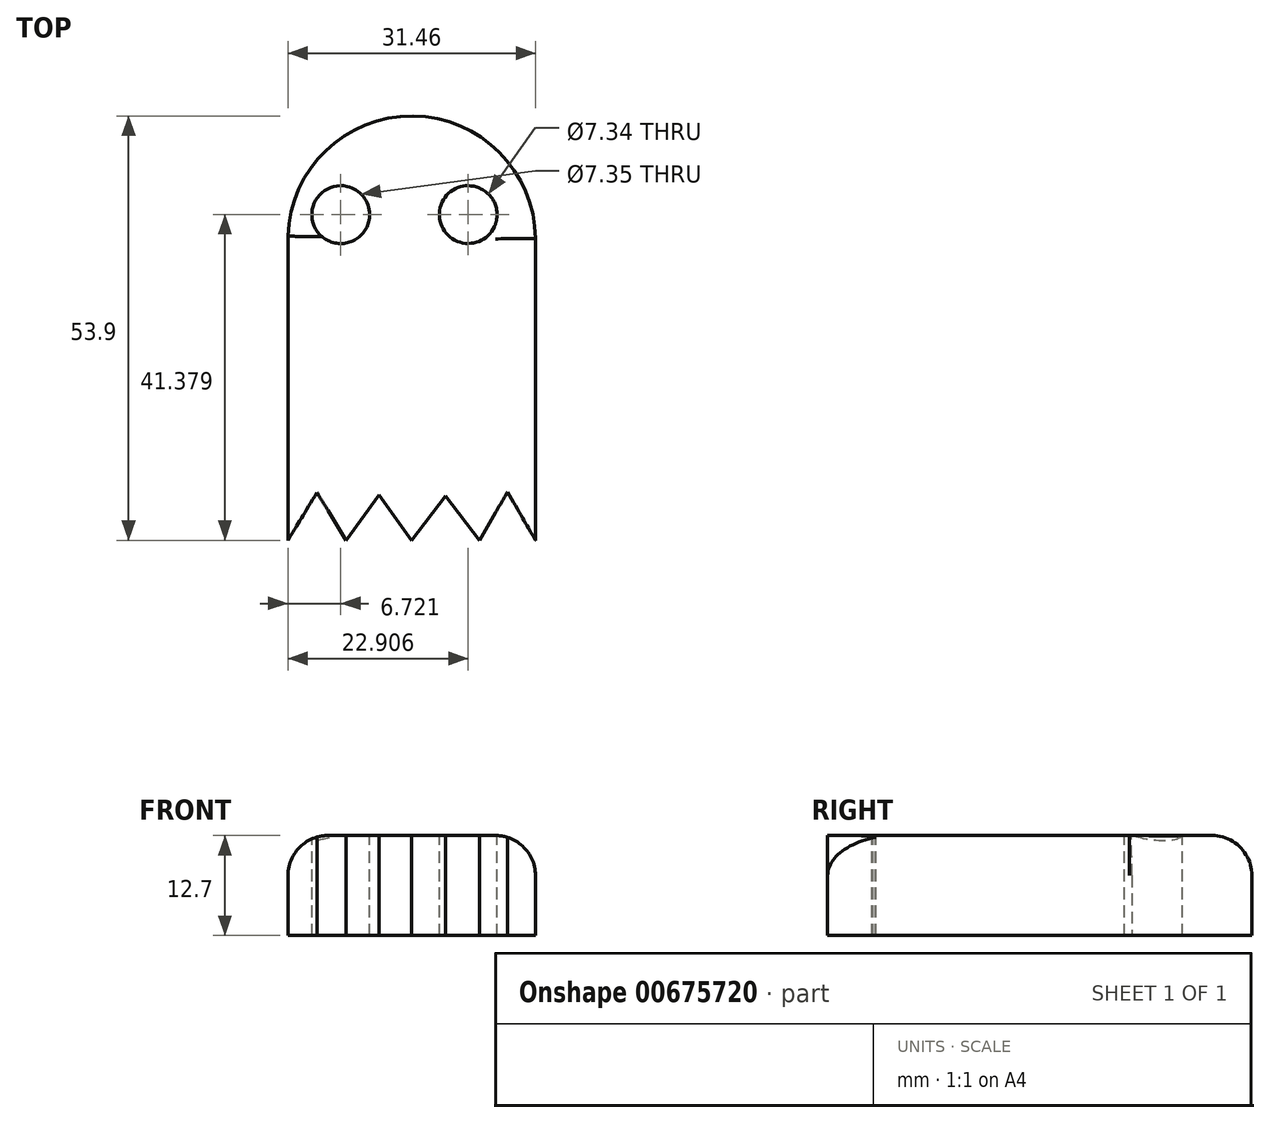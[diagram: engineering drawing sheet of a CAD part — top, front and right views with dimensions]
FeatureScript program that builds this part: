
annotation { "Feature Type Name" : "Feature", "Feature Type Description" : "" }
export const myFeature = defineFeature(function(context is Context, id is Id, definition is map)
    precondition{}
    {
        {
            var Q0;
            Q0=qCreatedBy(makeId("Top.planeOp"),FACE);
            var sketch = newSketch(context, id + "F0", { "sketchPlane" : qUnion([Q0])});
            skArc(sketch, "E0", {"start": v(-32.52, 38.33) * mm, "mid": v(-48.1, 53.9) * mm, "end": v(-63.98, 38.63) * mm});
            skLineSegment(sketch, "E1", {"start": v(-63.98, 38.63) * mm, "end": v(-63.98, 0) * mm});
            skLineSegment(sketch, "E2", {"start": v(-63.98, 0) * mm, "end": v(-32.52, 0) * mm});
            skLineSegment(sketch, "E3", {"start": v(-32.52, 0) * mm, "end": v(-32.52, 38.33) * mm});
            skSolve(sketch);
        }
        {
            var Q0;
            Q0=makeQuery(id+"F0.imprint","IMPRINT",FACE,{"disambiguationData":[TD([[makeQuery(id+"F0.imprint","IMPRINT",EDGE,{"derivedFrom":sQuery(id+"F0.wireOp",EDGE,"E0")}),1.0]])]});
            extrude(context, id + "F1", {"entities" : qUnion([Q0]), "depth" : 12.7 * mm, "offsetDistance" : 25.4 * mm});
        }
        {
            var Q0;
            Q0=makeQuery(id+"F1.opExtrude","CAP_FACE",FACE,{"disambiguationData":[OSD([sQuery(id+"F0.wireOp",EDGE,"E0"),sQuery(id+"F0.wireOp",EDGE,"E1"),sQuery(id+"F0.wireOp",EDGE,"E2"),sQuery(id+"F0.wireOp",EDGE,"E3")])],"isStart":false});
            var sketch = newSketch(context, id + "F2", { "sketchPlane" : qUnion([Q0])});
            skLineSegment(sketch, "E4", {"start": v(-56.58, 0) * mm, "end": v(-60.28, 6.08) * mm});
            skLineSegment(sketch, "E5", {"start": v(-60.28, 6.08) * mm, "end": v(-63.98, 0) * mm});
            skLineSegment(sketch, "E6", {"start": v(-56.58, 0) * mm, "end": v(-52.41, 5.77) * mm});
            skLineSegment(sketch, "E7", {"start": v(-52.41, 5.77) * mm, "end": v(-48.25, 0) * mm});
            skLineSegment(sketch, "E8", {"start": v(-56.58, 0) * mm, "end": v(-48.25, 0) * mm});
            skLineSegment(sketch, "E9", {"start": v(-48.25, 0) * mm, "end": v(-39.64, 0) * mm});
            skLineSegment(sketch, "E10", {"start": v(-48.25, 0) * mm, "end": v(-43.94, 5.66) * mm});
            skPoint(sketch, "E10.endSnap0", {"position": v(-43.94, 0) * mm});
            skLineSegment(sketch, "E11", {"start": v(-39.64, 0) * mm, "end": v(-43.94, 5.66) * mm});
            skLineSegment(sketch, "E12", {"start": v(-39.64, 0) * mm, "end": v(-36.08, 6.16) * mm});
            skLineSegment(sketch, "E13", {"start": v(-32.52, 0) * mm, "end": v(-36.08, 6.16) * mm});
            skLineSegment(sketch, "E14", {"start": v(-39.64, 0) * mm, "end": v(-32.52, 0) * mm});
            skLineSegment(sketch, "E15", {"start": v(-63.98, 0) * mm, "end": v(-56.58, 0) * mm});
            skSolve(sketch);
        }
        {
            var Q0;
            Q0=makeQuery(id+"F2.imprint","IMPRINT",FACE,{"disambiguationData":[TD([[makeQuery(id+"F2.imprint","IMPRINT",EDGE,{"derivedFrom":sQuery(id+"F2.wireOp",EDGE,"R8JNdmT0-IR0j-nOqT-kEw3-dpZqLVy3Gdbe")}),1.0]])]});
            var Q1;
            Q1=makeQuery(id+"F2.imprint","IMPRINT",FACE,{"disambiguationData":[TD([[makeQuery(id+"F2.imprint","IMPRINT",EDGE,{"derivedFrom":sQuery(id+"F2.wireOp",EDGE,"E6")}),-1.0]])]});
            var Q2;
            Q2=makeQuery(id+"F2.imprint","IMPRINT",FACE,{"disambiguationData":[TD([[makeQuery(id+"F2.imprint","IMPRINT",EDGE,{"derivedFrom":sQuery(id+"F2.wireOp",EDGE,"E9")}),1.0]])]});
            var Q3;
            Q3=makeQuery(id+"F2.imprint","IMPRINT",FACE,{"disambiguationData":[TD([[makeQuery(id+"F2.imprint","IMPRINT",EDGE,{"derivedFrom":sQuery(id+"F2.wireOp",EDGE,"E12")}),-1.0]])]});
            var Q4;
            Q4=makeQuery(id+"F2.imprint","IMPRINT",FACE,{"disambiguationData":[TD([[makeQuery(id+"F2.imprint","IMPRINT",EDGE,{"derivedFrom":sQuery(id+"F2.wireOp",EDGE,"E4")}),1.0]])]});
            extrude(context, id + "F3", {"entities" : qUnion([Q0, Q1, Q2, Q3, Q4]), "operationType" : NewBodyOperationType.REMOVE, "endBound" : BoundingType.THROUGH_ALL, "oppositeDirection" : true, "depth" : 25.4 * mm, "offsetDistance" : 25.4 * mm});
        }
        {
            var Q0;
            Q0=makeQuery(id+"F1.opExtrude","CAP_FACE",FACE,{"disambiguationData":[OSD([sQuery(id+"F0.wireOp",EDGE,"E0"),sQuery(id+"F0.wireOp",EDGE,"E1"),sQuery(id+"F0.wireOp",EDGE,"E2"),sQuery(id+"F0.wireOp",EDGE,"E3")])],"isStart":false});
            var sketch = newSketch(context, id + "F4", { "sketchPlane" : qUnion([Q0])});
            skCircle(sketch, "E16", {"center": v(-57.26, 41.38) * mm, "radius": 3.68 * mm});
            skCircle(sketch, "E17", {"center": v(-41.07, 41.38) * mm, "radius": 3.67 * mm});
            skPoint(sketch, "E18.end.orphan", {"position": v(-41.07, 45.05) * mm});
            skSolve(sketch);
        }
        {
            var Q0;
            Q0=makeQuery(id+"F4.imprint","IMPRINT",FACE,{"disambiguationData":[TD([[makeQuery(id+"F4.imprint","IMPRINT",EDGE,{"derivedFrom":sQuery(id+"F4.wireOp",EDGE,"E16")}),1.0]])]});
            var Q1;
            Q1=makeQuery(id+"F4.imprint","IMPRINT",FACE,{"disambiguationData":[TD([[makeQuery(id+"F4.imprint","IMPRINT",EDGE,{"derivedFrom":sQuery(id+"F4.wireOp",EDGE,"TzoXqbMI-gVJF-v2TF-hHPA-xfVAgKuncTeS")}),1.0]])]});
            var Q2;
            Q2=makeQuery(id+"F4.imprint","IMPRINT",FACE,{"disambiguationData":[TD([[makeQuery(id+"F4.imprint","IMPRINT",EDGE,{"derivedFrom":sQuery(id+"F4.wireOp",EDGE,"E17")}),1.0]])]});
            extrude(context, id + "F5", {"entities" : qUnion([Q0, Q1, Q2]), "operationType" : NewBodyOperationType.REMOVE, "endBound" : BoundingType.THROUGH_ALL, "oppositeDirection" : true, "depth" : 25.4 * mm, "offsetDistance" : 25.4 * mm});
        }
        {
            var Q0;
            Q0=makeQuery(id+"F1.opExtrude","CAP_EDGE",EDGE,{"disambiguationData":[OSD([sQuery(id+"F0.wireOp",EDGE,"E1")])],"isStart":false});
            var Q1;
            Q1=makeQuery(id+"F1.opExtrude","CAP_EDGE",EDGE,{"disambiguationData":[OSD([sQuery(id+"F0.wireOp",EDGE,"E3")])],"isStart":false});
            var Q2;
            Q2=makeQuery(id+"F1.opExtrude","CAP_EDGE",EDGE,{"disambiguationData":[OSD([sQuery(id+"F0.wireOp",EDGE,"E0")])],"isStart":false});
            fillet(context, id + "F6", {"entities" : qUnion([Q0, Q1, Q2]), "radius" : 5.08 * mm, "tangentPropagation" : true, "allowEdgeOverflow" : false});
        }
    });
